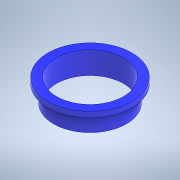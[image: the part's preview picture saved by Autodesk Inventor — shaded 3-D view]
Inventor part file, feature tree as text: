
AUTODESK INVENTOR PART (.ipt)
format: ipt  version: 2022 (Build 260153000, 153)  size: 118,784 bytes
history: native  units: mm
features: extrude x2, sketch x2
ambient origin geometry x8: Origin, YZ Plane, XZ Plane, XY Plane, X Axis, Y Axis, Z Axis, Center Point
bodies: Solid1 (feature_tree)
feature tree (4):
  extrude  "Extrusion1"  Depth=13.0mm
  extrude  "Extrusion2"  Depth=1.0mm
  sketch  "Sketch1"  dims[d0=12.0mm d1=13.0mm]
  sketch  "Sketch2"  dims[d2=3.0mm d3=0.0mm d4=15.0mm d5=1.0mm d6=0.0mm d7=12.0mm]
